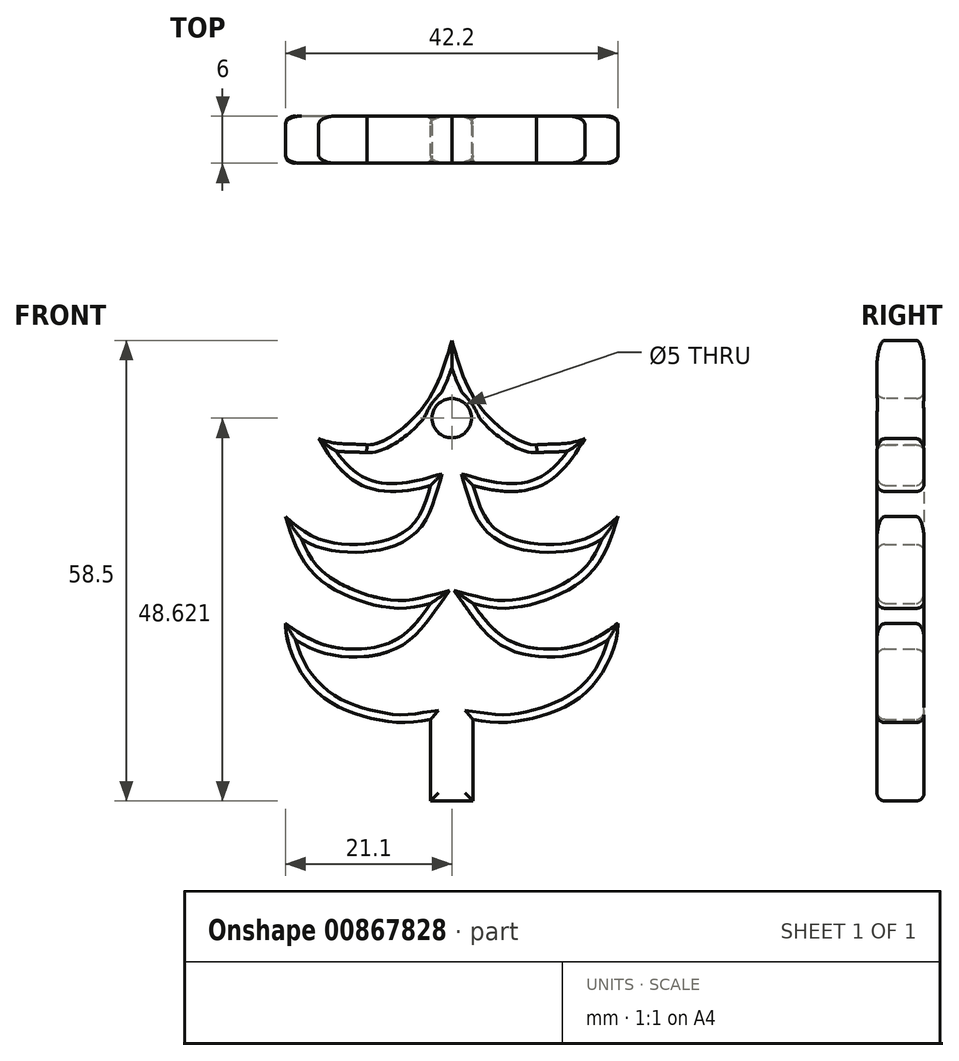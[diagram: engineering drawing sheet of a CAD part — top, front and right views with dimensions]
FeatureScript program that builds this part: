
annotation { "Feature Type Name" : "Feature", "Feature Type Description" : "" }
export const myFeature = defineFeature(function(context is Context, id is Id, definition is map)
    precondition{}
    {
        {
            var Q0;
            Q0=qCreatedBy(makeId("Front.planeOp"),FACE);
            var sketch = newSketch(context, id + "F0", { "sketchPlane" : qUnion([Q0])});
            skFitSpline(sketch, "E0", {"points": [v(0, 58.5) * mm, v(-2.7, 51.41) * mm, v(-7.22, 46.6) * mm, v(-10.77, 45.23) * mm, v(-13.74, 46) * mm], "startDerivative": vector(-7.03, -24.23) * mm, "endDerivative": vector(-13.44, 4.85) * mm});
            skFitSpline(sketch, "E1", {"points": [v(-16.9, 46) * mm, v(-11.2, 40) * mm, v(-2.7, 40.08) * mm], "startDerivative": vector(9.86, -16.68) * mm, "endDerivative": vector(18.47, 5.37) * mm});
            skFitSpline(sketch, "E2", {"points": [v(-16.9, 46) * mm, v(-10.77, 45.23) * mm], "startDerivative": vector(6.06, -2.65) * mm, "endDerivative": vector(5.67, -0.57) * mm});
            skFitSpline(sketch, "E3", {"points": [v(-2.7, 40.08) * mm, v(-6.1, 34.13) * mm, v(-16, 33) * mm, v(-21.1, 36.12) * mm], "startDerivative": vector(-6.36, -21.62) * mm, "endDerivative": vector(-14.13, 12.64) * mm});
            skFitSpline(sketch, "E4", {"points": [v(-21.1, 36.12) * mm, v(-17.14, 28.47) * mm, v(-7.5, 24.5) * mm, v(-2.7, 25.07) * mm], "startDerivative": vector(7.26, -23.82) * mm, "endDerivative": vector(16.04, 4.22) * mm});
            skFitSpline(sketch, "E5", {"points": [v(-2.7, 25.07) * mm, v(-7.5, 20.25) * mm, v(-15.72, 19.69) * mm, v(-21.1, 22.52) * mm], "startDerivative": vector(-12.22, -17.28) * mm, "endDerivative": vector(-15.47, 10.93) * mm});
            skFitSpline(sketch, "E6", {"points": [v(-21.1, 22.52) * mm, v(-17.18, 13.89) * mm, v(-8.76, 10.18) * mm, v(-2.7, 10.34) * mm], "startDerivative": vector(-0.11, -20.89) * mm, "endDerivative": vector(31.52, 5.02) * mm});
            skFitSpline(sketch, "E7", {"points": [v(-2.7, 10.34) * mm, v(-2.7, 0) * mm], "startDerivative": vector(0, -10.34) * mm, "endDerivative": vector(0, -10.34) * mm});
            skLineSegment(sketch, "E8", {"start": v(-2.7, 0) * mm, "end": v(0, 0) * mm});
            skFitSpline(sketch, "E9.MirrorCS", {"points": [v(16.9, 46) * mm, v(10.77, 45.23) * mm], "startDerivative": vector(-6.06, -2.65) * mm, "endDerivative": vector(-5.67, -0.57) * mm});
            skLineSegment(sketch, "E10.MirrorCS", {"start": v(2.7, 0) * mm, "end": v(0, 0) * mm});
            skFitSpline(sketch, "E11.MirrorCS", {"points": [v(2.7, 10.34) * mm, v(2.7, 0) * mm], "startDerivative": vector(0, -10.34) * mm, "endDerivative": vector(0, -10.34) * mm});
            skFitSpline(sketch, "E12.MirrorCS", {"points": [v(16.9, 46) * mm, v(11.2, 40) * mm, v(2.7, 40.08) * mm], "startDerivative": vector(-9.86, -16.68) * mm, "endDerivative": vector(-18.47, 5.37) * mm});
            skFitSpline(sketch, "E13.MirrorCS", {"points": [v(2.7, 25.07) * mm, v(7.5, 20.25) * mm, v(15.72, 19.69) * mm, v(21.1, 22.52) * mm], "startDerivative": vector(12.22, -17.28) * mm, "endDerivative": vector(15.47, 10.93) * mm});
            skFitSpline(sketch, "E14.MirrorCS", {"points": [v(2.7, 40.08) * mm, v(6.1, 34.13) * mm, v(16, 33) * mm, v(21.1, 36.12) * mm], "startDerivative": vector(6.36, -21.62) * mm, "endDerivative": vector(14.13, 12.64) * mm});
            skFitSpline(sketch, "E15.MirrorCS", {"points": [v(21.1, 36.12) * mm, v(17.14, 28.47) * mm, v(7.5, 24.5) * mm, v(2.7, 25.07) * mm], "startDerivative": vector(-7.26, -23.82) * mm, "endDerivative": vector(-16.04, 4.22) * mm});
            skFitSpline(sketch, "E16.MirrorCS", {"points": [v(21.1, 22.52) * mm, v(17.18, 13.89) * mm, v(8.76, 10.18) * mm, v(2.7, 10.34) * mm], "startDerivative": vector(0.11, -20.89) * mm, "endDerivative": vector(-31.52, 5.02) * mm});
            skFitSpline(sketch, "E17.MirrorCS", {"points": [v(0, 58.5) * mm, v(2.7, 51.41) * mm, v(7.22, 46.6) * mm, v(10.77, 45.23) * mm, v(13.74, 46) * mm], "startDerivative": vector(7.03, -24.23) * mm, "endDerivative": vector(13.44, 4.85) * mm});
            skSolve(sketch);
        }
        {
            var Q0;
            Q0 = qSketchRegion(id + "F0", true);
            extrude(context, id + "F1", {"entities" : qUnion([Q0]), "depth" : 6 * mm, "offsetDistance" : 25 * mm});
        }
        {
            var Q0;
            Q0=makeQuery(id+"F1.opExtrude","CAP_FACE",FACE,{"disambiguationData":[OSD([sQuery(id+"F0.wireOp",EDGE,"E0"),sQuery(id+"F0.wireOp",EDGE,"E1"),sQuery(id+"F0.wireOp",EDGE,"E2"),sQuery(id+"F0.wireOp",EDGE,"E3"),sQuery(id+"F0.wireOp",EDGE,"E4"),sQuery(id+"F0.wireOp",EDGE,"E5"),sQuery(id+"F0.wireOp",EDGE,"E6"),sQuery(id+"F0.wireOp",EDGE,"E7"),sQuery(id+"F0.wireOp",EDGE,"E8"),sQuery(id+"F0.wireOp",EDGE,"E9.MirrorCS"),sQuery(id+"F0.wireOp",EDGE,"E10.MirrorCS"),sQuery(id+"F0.wireOp",EDGE,"E11.MirrorCS"),sQuery(id+"F0.wireOp",EDGE,"E12.MirrorCS"),sQuery(id+"F0.wireOp",EDGE,"E13.MirrorCS"),sQuery(id+"F0.wireOp",EDGE,"E14.MirrorCS"),sQuery(id+"F0.wireOp",EDGE,"E15.MirrorCS"),sQuery(id+"F0.wireOp",EDGE,"E16.MirrorCS"),sQuery(id+"F0.wireOp",EDGE,"E17.MirrorCS")])],"isStart":false});
            var sketch = newSketch(context, id + "F2", { "sketchPlane" : qUnion([Q0])});
            skCircle(sketch, "E18", {"center": v(0, 48.62) * mm, "radius": 2.5 * mm});
            skSolve(sketch);
        }
        {
            var Q0;
            Q0 = qSketchRegion(id + "F2", true);
            extrude(context, id + "F3", {"entities" : qUnion([Q0]), "operationType" : NewBodyOperationType.REMOVE, "oppositeDirection" : true, "depth" : 25 * mm, "offsetDistance" : 25 * mm});
        }
        {
            var Q0;
            Q0=makeQuery(id+"F1.opExtrude","CAP_FACE",FACE,{"disambiguationData":[OSD([sQuery(id+"F0.wireOp",EDGE,"E0"),sQuery(id+"F0.wireOp",EDGE,"E1"),sQuery(id+"F0.wireOp",EDGE,"E2"),sQuery(id+"F0.wireOp",EDGE,"E3"),sQuery(id+"F0.wireOp",EDGE,"E4"),sQuery(id+"F0.wireOp",EDGE,"E5"),sQuery(id+"F0.wireOp",EDGE,"E6"),sQuery(id+"F0.wireOp",EDGE,"E7"),sQuery(id+"F0.wireOp",EDGE,"E8"),sQuery(id+"F0.wireOp",EDGE,"E9.MirrorCS"),sQuery(id+"F0.wireOp",EDGE,"E10.MirrorCS"),sQuery(id+"F0.wireOp",EDGE,"E11.MirrorCS"),sQuery(id+"F0.wireOp",EDGE,"E12.MirrorCS"),sQuery(id+"F0.wireOp",EDGE,"E13.MirrorCS"),sQuery(id+"F0.wireOp",EDGE,"E14.MirrorCS"),sQuery(id+"F0.wireOp",EDGE,"E15.MirrorCS"),sQuery(id+"F0.wireOp",EDGE,"E16.MirrorCS"),sQuery(id+"F0.wireOp",EDGE,"E17.MirrorCS")])],"isStart":false});
            var Q1;
            Q1=makeQuery(id+"F1.opExtrude","CAP_FACE",FACE,{"disambiguationData":[OSD([sQuery(id+"F0.wireOp",EDGE,"E0"),sQuery(id+"F0.wireOp",EDGE,"E1"),sQuery(id+"F0.wireOp",EDGE,"E2"),sQuery(id+"F0.wireOp",EDGE,"E3"),sQuery(id+"F0.wireOp",EDGE,"E4"),sQuery(id+"F0.wireOp",EDGE,"E5"),sQuery(id+"F0.wireOp",EDGE,"E6"),sQuery(id+"F0.wireOp",EDGE,"E7"),sQuery(id+"F0.wireOp",EDGE,"E8"),sQuery(id+"F0.wireOp",EDGE,"E9.MirrorCS"),sQuery(id+"F0.wireOp",EDGE,"E10.MirrorCS"),sQuery(id+"F0.wireOp",EDGE,"E11.MirrorCS"),sQuery(id+"F0.wireOp",EDGE,"E12.MirrorCS"),sQuery(id+"F0.wireOp",EDGE,"E13.MirrorCS"),sQuery(id+"F0.wireOp",EDGE,"E14.MirrorCS"),sQuery(id+"F0.wireOp",EDGE,"E15.MirrorCS"),sQuery(id+"F0.wireOp",EDGE,"E16.MirrorCS"),sQuery(id+"F0.wireOp",EDGE,"E17.MirrorCS")])],"isStart":true});
            fillet(context, id + "F4", {"entities" : qUnion([Q0, Q1]), "radius" : 1 * mm, "tangentPropagation" : true, "allowEdgeOverflow" : false});
        }
    });
